# Revit family: Siella_G5 300x1200
name_source: partatom
category: Lighting Fixtures
revit_build: Autodesk Revit 2018 (Build: 20190510_1515(x64)
units: mm (PartAtom-declared; Revit-internal decimal feet)

## family parameters
Cut with Voids When Loaded = No
Host = Face
Light Source = No
OmniClass Number = 23.80.70.14
OmniClass Title = Luminaries for External Lighting
Part Type = Normal
Room Calculation Point = No
Round Connector Dimension = Use Diameter
Shared = Yes

## types (2) — shared parameters
Apparent Load = 33 VA
CENFluxCode = 58 86 97 100 100 0 0 0 0
CRI = 80
Color = RAL9016 Verkehrsweiß
Colour temperature (K) = 4000
Connection Load = 33 VA
Degree of protection = IP40
LS_offset = 1 mm  [stored 0.00328084 ft]
Lamp = LED
Lamp_0 = LED
Light Source = Siella_G5_LS : TX060597
Luminous flux of luminaire (lm) = 3600
Manufacturer = TRILUX
Mat = TRILUX_RAL9016
SEO = TRILUX_WH_4000
Safety class = I
URL = http://www.trilux.com
h = 13 mm  [stored 0.0426509 ft]
l = 295 mm
l_offset = 247 mm
w = 1195 mm  [stored 3.9206 ft]
w_offset = 1147 mm
zero-valued in all types: Default Elevation

## per-type parameters (varying)
| type | Dimming/Balast | TK | TOC | Weight |
| Siella G5 M46 OTA19 LED3600-840 ETDD | ETDD | 10175396 | 7165451 | 2.3 |
| Siella G5 M46 OTA19 LED3600-840 ET | ET | 10175395 | 7165440 | 2.1 |

note: [stored X ft] marks values corroborated as IEEE doubles in the binary element streams (Revit-internal decimal feet)

## geometry (parser evidence)
native form markers: Sweep x4
no freeform markers — native parametric forms only
